FCSTD DOCUMENT  (FreeCAD 1.0R39109 (Git))
Label: cs_f1m
License: All rights reserved
LicenseURL: https://en.wikipedia.org/wiki/All_rights_reserved
objects: Sketcher::SketchObject×1, PartDesign::Body×1
note: 3 computed .brp shape members not serialized (recipe doc carries the construction recipe); baked Part::Feature solids carry a one-line shape summary decoded from their .brp

FEATURE [Sketcher::SketchObject] Sketch
  ArcFitTolerance = 1e-06
  AttachmentSupport = -> [XY_Plane]
  FullyConstrained = true
  MakeInternals = false
  MapMode = 5
  sketch-geometry (56):
    g0: LineSegment [constr] StartX=2 StartY=0 StartZ=0 EndX=835 EndY=0 EndZ=0
    g1: LineSegment [constr] StartX=836.972 StartY=1.9998 StartZ=0 EndX=830.028 EndY=498 EndZ=0
    g2: LineSegment [constr] StartX=828 StartY=500 StartZ=0 EndX=2 EndY=500 EndZ=0
    g3: LineSegment [constr] StartX=0 StartY=498 StartZ=0 EndX=0 EndY=2 EndZ=0
    g4: LineSegment StartX=125 StartY=390 StartZ=0 EndX=125 EndY=90 EndZ=0
    g5: LineSegment StartX=725 StartY=90 StartZ=0 EndX=725 EndY=390 EndZ=0
    g6: ArcOfCircle CenterX=175 CenterY=390 CenterZ=0 NormalX=0 NormalY=0 NormalZ=1 AngleXU=0 Radius=50 StartAngle=1.5708 EndAngle=3.14159
    g7: GeomPoint [constr] X=125 Y=375 Z=0
    g8: ArcOfCircle CenterX=175 CenterY=90 CenterZ=0 NormalX=0 NormalY=0 NormalZ=1 AngleXU=0 Radius=50 StartAngle=3.14159 EndAngle=4.71239
    g9: GeomPoint [constr] X=125 Y=95 Z=0
    g10: ArcOfCircle CenterX=675 CenterY=90 CenterZ=0 NormalX=0 NormalY=0 NormalZ=1 AngleXU=0 Radius=50 StartAngle=4.71239 EndAngle=6.28319
    g11: ArcOfCircle CenterX=675 CenterY=390 CenterZ=0 NormalX=0 NormalY=0 NormalZ=1 AngleXU=0 Radius=50 StartAngle=0 EndAngle=1.5708
    g12: LineSegment StartX=175 StartY=440 StartZ=0 EndX=675 EndY=440 EndZ=0
    g13: LineSegment StartX=175 StartY=40 StartZ=0 EndX=675 EndY=40 EndZ=0
    g14: ArcOfCircle [constr] CenterX=2 CenterY=498 CenterZ=0 NormalX=0 NormalY=0 NormalZ=1 AngleXU=0 Radius=2 StartAngle=1.5708 EndAngle=3.14159
    g15: GeomPoint [constr] X=0 Y=500 Z=0
    g16: ArcOfCircle [constr] CenterX=2 CenterY=2 CenterZ=0 NormalX=0 NormalY=0 NormalZ=1 AngleXU=0 Radius=2 StartAngle=3.14159 EndAngle=4.71239
    g17: GeomPoint [constr] X=0 Y=0 Z=0
    g18: ArcOfCircle [constr] CenterX=835 CenterY=1.9722 CenterZ=0 NormalX=0 NormalY=0 NormalZ=1 AngleXU=0 Radius=1.9722 StartAngle=4.71239 EndAngle=6.29718
    g19: GeomPoint [constr] X=837 Y=0 Z=0
    g20: ArcOfCircle [constr] CenterX=828 CenterY=497.972 CenterZ=0 NormalX=0 NormalY=0 NormalZ=1 AngleXU=0 Radius=2.0282 StartAngle=0.0139991 EndAngle=1.5708
    g21: GeomPoint [constr] X=830 Y=500 Z=0
    g22: Circle [constr] CenterX=134 CenterY=104 CenterZ=0 NormalX=0 NormalY=0 NormalZ=1 AngleXU=0 Radius=1.5
    g23: Circle [constr] CenterX=134 CenterY=366 CenterZ=0 NormalX=0 NormalY=0 NormalZ=1 AngleXU=0 Radius=1.5
    g24: Circle [constr] CenterX=32 CenterY=487.972 CenterZ=0 NormalX=0 NormalY=0 NormalZ=1 AngleXU=0 Radius=1.5
    g25: Circle [constr] CenterX=415 CenterY=487.972 CenterZ=0 NormalX=0 NormalY=0 NormalZ=1 AngleXU=0 Radius=1.5
    g26: Circle [constr] CenterX=798 CenterY=487.972 CenterZ=0 NormalX=0 NormalY=0 NormalZ=1 AngleXU=0 Radius=1.5
    g27: Circle [constr] CenterX=820 CenterY=250 CenterZ=0 NormalX=0 NormalY=0 NormalZ=1 AngleXU=0 Radius=1.5
    g28: Circle [constr] CenterX=807 CenterY=10 CenterZ=0 NormalX=0 NormalY=0 NormalZ=1 AngleXU=0 Radius=1.5
    g29: Circle [constr] CenterX=418.5 CenterY=10 CenterZ=0 NormalX=0 NormalY=0 NormalZ=1 AngleXU=0 Radius=1.5
    g30: Circle [constr] CenterX=30 CenterY=10 CenterZ=0 NormalX=0 NormalY=0 NormalZ=1 AngleXU=0 Radius=1.5
    g31: Circle [constr] CenterX=10 CenterY=250 CenterZ=0 NormalX=0 NormalY=0 NormalZ=1 AngleXU=0 Radius=1.5
    g32: Circle [constr] CenterX=40 CenterY=400 CenterZ=0 NormalX=0 NormalY=0 NormalZ=1 AngleXU=0 Radius=8.5
    g33: Circle [constr] CenterX=80 CenterY=400 CenterZ=0 NormalX=0 NormalY=0 NormalZ=1 AngleXU=0 Radius=8.5
    g34: Circle [constr] CenterX=40 CenterY=350 CenterZ=0 NormalX=0 NormalY=0 NormalZ=1 AngleXU=0 Radius=8.5
    g35: Circle [constr] CenterX=80 CenterY=350 CenterZ=0 NormalX=0 NormalY=0 NormalZ=1 AngleXU=0 Radius=8.5
    g36: Circle [constr] CenterX=40 CenterY=300 CenterZ=0 NormalX=0 NormalY=0 NormalZ=1 AngleXU=0 Radius=8.5
    g37: Circle [constr] CenterX=80 CenterY=300 CenterZ=0 NormalX=0 NormalY=0 NormalZ=1 AngleXU=0 Radius=8.5
    g38: Circle [constr] CenterX=40 CenterY=250 CenterZ=0 NormalX=0 NormalY=0 NormalZ=1 AngleXU=0 Radius=8.5
    g39: Circle [constr] CenterX=80 CenterY=250 CenterZ=0 NormalX=0 NormalY=0 NormalZ=1 AngleXU=0 Radius=8.5
    g40: LineSegment [constr] StartX=135 StartY=88 StartZ=0 EndX=135 EndY=388 EndZ=0
    g41: LineSegment [constr] StartX=175 StartY=428 StartZ=0 EndX=675 EndY=428 EndZ=0
    g42: LineSegment [constr] StartX=715 StartY=388 StartZ=0 EndX=715 EndY=88 EndZ=0
    g43: LineSegment [constr] StartX=675 StartY=48 StartZ=0 EndX=175 EndY=48 EndZ=0
    g44: ArcOfCircle [constr] CenterX=175 CenterY=388 CenterZ=0 NormalX=0 NormalY=0 NormalZ=1 AngleXU=0 Radius=40 StartAngle=1.5708 EndAngle=3.14159
    g45: GeomPoint [constr] X=135 Y=428 Z=0
    g46: ArcOfCircle [constr] CenterX=175 CenterY=88 CenterZ=0 NormalX=0 NormalY=0 NormalZ=1 AngleXU=0 Radius=40 StartAngle=3.14159 EndAngle=4.71239
    g47: GeomPoint [constr] X=135 Y=48 Z=0
    g48: ArcOfCircle [constr] CenterX=675 CenterY=88 CenterZ=0 NormalX=0 NormalY=0 NormalZ=1 AngleXU=0 Radius=40 StartAngle=4.71239 EndAngle=6.28319
    g49: GeomPoint [constr] X=715 Y=48 Z=0
    g50: ArcOfCircle [constr] CenterX=675 CenterY=388 CenterZ=0 NormalX=0 NormalY=0 NormalZ=1 AngleXU=0 Radius=40 StartAngle=3e-16 EndAngle=1.5708
    g51: GeomPoint [constr] X=715 Y=428 Z=0
    g52: Circle CenterX=155 CenterY=408 CenterZ=0 NormalX=0 NormalY=0 NormalZ=1 AngleXU=0 Radius=1.5
    g53: Circle CenterX=155 CenterY=68 CenterZ=0 NormalX=0 NormalY=0 NormalZ=1 AngleXU=0 Radius=1.5
    g54: Circle CenterX=695 CenterY=68 CenterZ=0 NormalX=0 NormalY=0 NormalZ=1 AngleXU=0 Radius=1.5
    g55: Circle CenterX=695 CenterY=408 CenterZ=0 NormalX=0 NormalY=0 NormalZ=1 AngleXU=0 Radius=1.5
  constraints (148):
    c: Horizontal(g0)
    c: Horizontal(g2)
    c: Vertical(g3)
    c: Distance(g19,g17) = 837
    c: Distance(g17,g15) = 500
    c: Coincident(g17,g-1)
    c: DistanceX(g15,g21) = 830
    c: Vertical(g4)
    c: Vertical(g5)
    c: DistanceY(g7,g15) = 125
    c: DistanceY(g9,g7) = 280
    c: DistanceX(g15,g7) = 125
    c: PointOnObject(g7,g4)
    c: Tangent(g4,g6) = -1.5708
    c: PointOnObject(g9,g4)
    c: Tangent(g4,g8) = -1.5708
    c: Tangent(g5,g10) = -1.5708
    c: Tangent(g5,g11) = -1.5708
    c: DistanceX(g7,g6) = 50
    c: DistanceX(g9,g8) = 50
    c: Coincident(g12,g6)
    c: Coincident(g12,g11)
    c: Horizontal(g12)
    c: Tangent(g13,g8) = -1.5708
    c: Coincident(g13,g10)
    c: Horizontal(g13)
    c: PointOnObject(g15,g2)
    c: PointOnObject(g15,g3)
    c: Tangent(g2,g14) = -1.5708
    c: Tangent(g3,g14) = -1.5708
    c: DistanceX(g15,g14) = 2
    c: PointOnObject(g17,g0)
    c: PointOnObject(g17,g3)
    c: Tangent(g0,g16) = -1.5708
    c: Tangent(g3,g16) = -1.5708
    c: PointOnObject(g19,g0)
    c: PointOnObject(g19,g1)
    c: Tangent(g0,g18) = -1.5708
    c: Tangent(g1,g18) = -1.5708
    c: PointOnObject(g21,g1)
    c: PointOnObject(g21,g2)
    c: Tangent(g1,g20) = -1.5708
    c: Tangent(g2,g20) = -1.5708
    c: DistanceX(g20,g21) = 2
    c: DistanceX(g18,g19) = 2
    c: DistanceX(g17,g16) = 2
    c: Diameter(g22) = 3
    c: Diameter(g23) = 3
    c: DistanceX(g7,g23) = 9
    c: DistanceY(g23,g7) = 9
    c: DistanceY(g9,g22) = 9
    c: DistanceX(g9,g22) = 9
    c: Diameter(g24) = 3
    c: Diameter(g25) = 3
    c: Diameter(g26) = 3
    c: Diameter(g27) = 3
    c: Diameter(g28) = 3
    c: Diameter(g29) = 3
    c: Diameter(g30) = 3
    c: Diameter(g31) = 3
    c: DistanceY(g25,g24) = 0
    c: DistanceY(g26,g25) = 0
    c: DistanceY(g26,g20) = 10
    c: DistanceX(g26,g20) = 30
    c: DistanceX(g14,g24) = 30
    c: DistanceX(g15,g25) = 415
    c: DistanceX(g17,g31) = 10
    c: DistanceY(g17,g31) = 250
    c: DistanceY(g17,g30) = 10
    c: DistanceY(g30,g29) = 0
    c: DistanceY(g29,g28) = 0
    c: DistanceX(g28,g19) = 30
    c: DistanceX(g29,g19) = 418.5
    c: DistanceX(g17,g30) = 30
    c: DistanceX(g27,g21) = 10
    c: DistanceY(g19,g27) = 250
    c: Diameter(g32) = 17
    c: Diameter(g33) = 17
    c: Diameter(g34) = 17
    c: Diameter(g35) = 17
    c: Diameter(g36) = 17
    c: Diameter(g37) = 17
    c: Diameter(g38) = 17
    c: Diameter(g39) = 17
    c: DistanceY(g38,g39) = 0
    c: DistanceY(g36,g37) = 0
    c: DistanceY(g35,g34) = 0
    c: DistanceY(g33,g32) = 0
    c: DistanceY(g34,g32) = 50
    c: DistanceY(g36,g34) = 50
    c: DistanceY(g38,g36) = 50
    c: DistanceX(g36,g38) = 0
    c: DistanceX(g34,g36) = 0
    c: DistanceX(g32,g34) = 0
    c: DistanceY(g32,g15) = 100
    c: DistanceX(g32,g33) = 40
    c: DistanceX(g34,g35) = 40
    c: DistanceX(g37,g35) = 0
    c: DistanceX(g39,g37) = 0
    c: DistanceX(g14,g38) = 40
    c: DistanceY(g4,g4) = 300
    c: DistanceX(g7,g6) = 50
    c: DistanceX(g10,g5) = 50
    c: DistanceY(g5,g5) = 300
    c: DistanceY(g6,g15) = 60
    c: DistanceX(g13,g13) = 500
    c: DistanceX(g10,g10) = 0
    c: DistanceX(g11,g11) = 0
    c: Vertical(g40)
    c: Vertical(g42)
    c: Horizontal(g41)
    c: Horizontal(g43)
    c: PointOnObject(g45,g41)
    c: PointOnObject(g45,g40)
    c: Tangent(g41,g44) = 1.5708
    c: Tangent(g40,g44) = 1.5708
    c: PointOnObject(g47,g43)
    c: PointOnObject(g47,g40)
    c: Tangent(g43,g46) = 1.5708
    c: Tangent(g40,g46) = 1.5708
    c: PointOnObject(g49,g43)
    c: PointOnObject(g49,g42)
    c: Tangent(g43,g48) = 1.5708
    c: Tangent(g42,g48) = 1.5708
    c: PointOnObject(g51,g42)
    c: PointOnObject(g51,g41)
    c: Tangent(g42,g50) = 1.5708
    c: Tangent(g41,g50) = 1.5708
    c: DistanceX(g47,g8) = 40
    c: DistanceX(g48,g49) = 40
    c: DistanceX(g11,g51) = 40
    c: DistanceX(g45,g44) = 40
    c: DistanceX(g43,g43) = 500
    c: DistanceX(g41,g41) = 500
    c: DistanceY(g40,g40) = 300
    c: DistanceY(g8,g43) = 8
    c: Diameter(g52) = 3
    c: Diameter(g53) = 3
    c: Diameter(g54) = 3
    c: Diameter(g55) = 3
    c: DistanceX(g55,g51) = 20
    c: DistanceY(g55,g51) = 20
    c: DistanceY(g49,g54) = 20
    c: DistanceX(g54,g49) = 20
    c: DistanceX(g47,g53) = 20
    c: DistanceY(g47,g53) = 20
    c: DistanceY(g52,g45) = 20
    c: DistanceX(g45,g52) = 20
FEATURE [PartDesign::Body] Body
  AllowCompound = false
  Group = -> [Sketch]
  Origin = -> Origin
